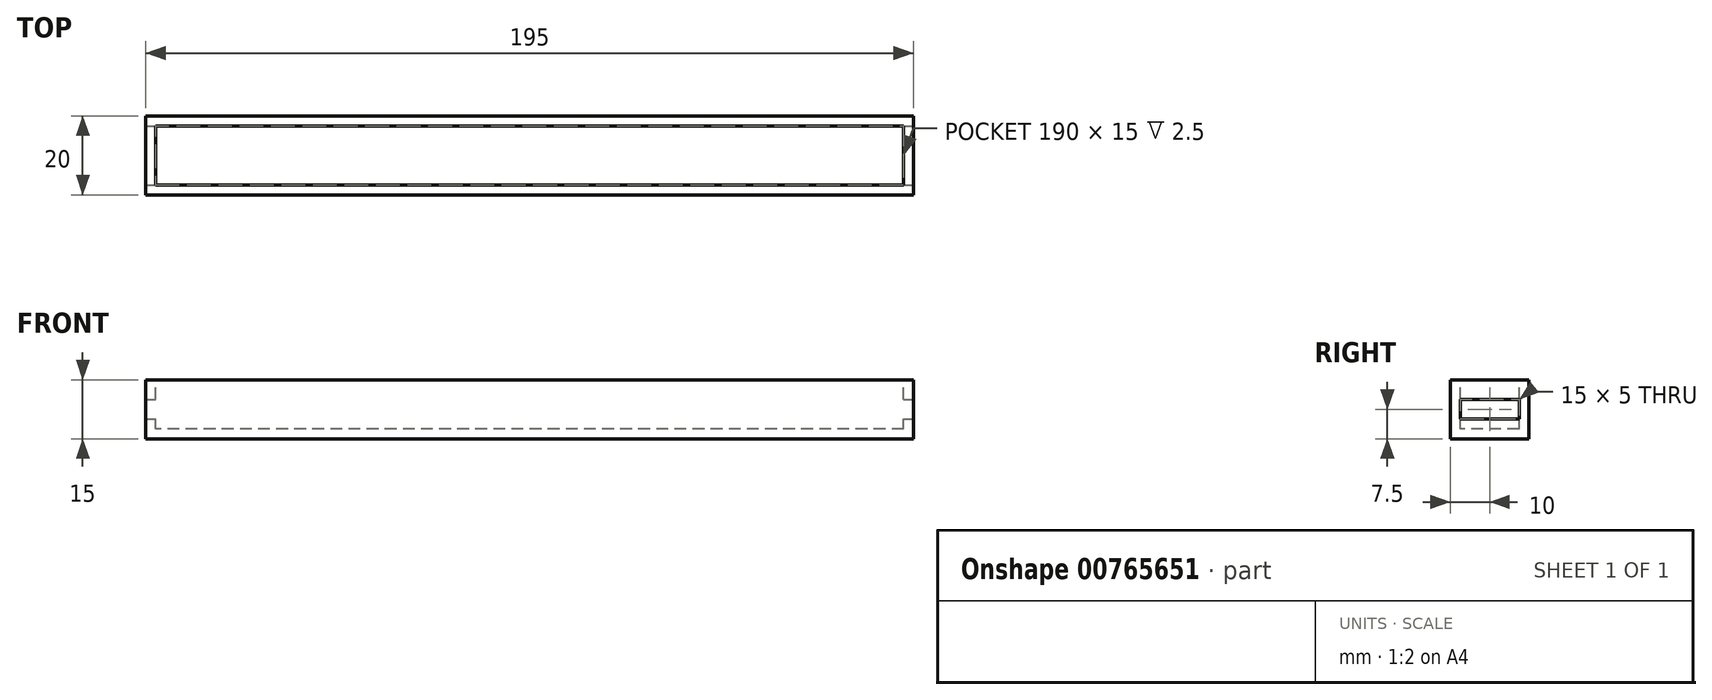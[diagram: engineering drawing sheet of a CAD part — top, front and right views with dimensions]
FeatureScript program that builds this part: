
annotation { "Feature Type Name" : "Feature", "Feature Type Description" : "" }
export const myFeature = defineFeature(function(context is Context, id is Id, definition is map)
    precondition{}
    {
        {
            var Q0;
            Q0=qCreatedBy(makeId("Top.planeOp"),FACE);
            var sketch = newSketch(context, id + "F0", { "sketchPlane" : qUnion([Q0])});
            skLineSegment(sketch, "E0.bottom", {"start": v(111.5, 111.5) * mm, "end": v(-111.5, 111.5) * mm});
            skLineSegment(sketch, "E0.top", {"start": v(111.5, -111.5) * mm, "end": v(-111.5, -111.5) * mm});
            skLineSegment(sketch, "E0.left", {"start": v(111.5, 111.5) * mm, "end": v(111.5, -111.5) * mm});
            skLineSegment(sketch, "E0.right", {"start": v(-111.5, 111.5) * mm, "end": v(-111.5, -111.5) * mm});
            skPoint(sketch, "E0.middle", {"position": v(0, 0) * mm});
            skLineSegment(sketch, "E1.bottom", {"start": v(-97.5, 10) * mm, "end": v(97.5, 10) * mm});
            skLineSegment(sketch, "E1.top", {"start": v(-97.5, -10) * mm, "end": v(97.5, -10) * mm});
            skLineSegment(sketch, "E1.left", {"start": v(-97.5, 10) * mm, "end": v(-97.5, -10) * mm});
            skLineSegment(sketch, "E1.right", {"start": v(97.5, 10) * mm, "end": v(97.5, -10) * mm});
            skSolve(sketch);
        }
        {
            var Q0;
            Q0=makeQuery(id+"F0.imprint","IMPRINT",FACE,{"disambiguationData":[TD([[makeQuery(id+"F0.imprint","IMPRINT",EDGE,{"derivedFrom":sQuery(id+"F0.wireOp",EDGE,"E1.bottom")}),-1.0]])]});
            extrude(context, id + "F1", {"entities" : qUnion([Q0]), "depth" : 15 * mm, "offsetDistance" : 25 * mm});
        }
        {
            var Q0;
            Q0=makeQuery(id+"F1.opExtrude","CAP_FACE",FACE,{"disambiguationData":[OSD([sQuery(id+"F0.wireOp",EDGE,"E1.bottom"),sQuery(id+"F0.wireOp",EDGE,"E1.top"),sQuery(id+"F0.wireOp",EDGE,"E1.left"),sQuery(id+"F0.wireOp",EDGE,"E1.right")])],"isStart":false});
            var sketch = newSketch(context, id + "F2", { "sketchPlane" : qUnion([Q0])});
            skLineSegment(sketch, "E2.bottom", {"start": v(95, 7.5) * mm, "end": v(-95, 7.5) * mm});
            skLineSegment(sketch, "E2.top", {"start": v(95, -7.5) * mm, "end": v(-95, -7.5) * mm});
            skLineSegment(sketch, "E2.left", {"start": v(95, 7.5) * mm, "end": v(95, -7.5) * mm});
            skLineSegment(sketch, "E2.right", {"start": v(-95, 7.5) * mm, "end": v(-95, -7.5) * mm});
            skPoint(sketch, "E2.middle", {"position": v(0, 0) * mm});
            skSolve(sketch);
        }
        {
            var Q0;
            Q0 = qSketchRegion(id + "F2", true);
            extrude(context, id + "F3", {"entities" : qUnion([Q0]), "operationType" : NewBodyOperationType.REMOVE, "oppositeDirection" : true, "depth" : 12.5 * mm, "offsetDistance" : 25 * mm});
        }
        {
            var Q0;
            Q0=makeQuery(id+"F1.opExtrude","SWEPT_FACE",FACE,{"disambiguationData":[OSD([sQuery(id+"F0.wireOp",EDGE,"E1.right")])]});
            var sketch = newSketch(context, id + "F4", { "sketchPlane" : qUnion([Q0])});
            skLineSegment(sketch, "E3.bottom", {"start": v(7.5, 10) * mm, "end": v(-7.5, 10) * mm});
            skLineSegment(sketch, "E3.top", {"start": v(7.5, 5) * mm, "end": v(-7.5, 5) * mm});
            skLineSegment(sketch, "E3.left", {"start": v(7.5, 10) * mm, "end": v(7.5, 5) * mm});
            skLineSegment(sketch, "E3.right", {"start": v(-7.5, 10) * mm, "end": v(-7.5, 5) * mm});
            skPoint(sketch, "E3.middle", {"position": v(0, 7.5) * mm});
            skSolve(sketch);
        }
        {
            var Q0;
            Q0=makeQuery(id+"F4.imprint","IMPRINT",FACE,{"disambiguationData":[TD([[makeQuery(id+"F4.imprint","IMPRINT",EDGE,{"derivedFrom":sQuery(id+"F4.wireOp",EDGE,"E3.bottom")}),1.0]])]});
            extrude(context, id + "F5", {"entities" : qUnion([Q0]), "operationType" : NewBodyOperationType.REMOVE, "endBound" : BoundingType.THROUGH_ALL, "oppositeDirection" : true, "depth" : 25 * mm, "offsetDistance" : 25 * mm});
        }
    });
